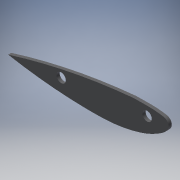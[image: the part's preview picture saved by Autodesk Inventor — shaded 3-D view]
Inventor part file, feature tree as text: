
AUTODESK INVENTOR PART (.ipt)
format: ipt  version: 2018.2 (Build 222227000, 227)  size: 130,560 bytes
history: native  units: mm
features: extrude x2, sketch x2, other x1, projected_geometry x1
ambient origin geometry x8: Origin, YZ Plane, XZ Plane, XY Plane, X Axis, Y Axis, Z Axis, Center Point
bodies: Body1 (feature_tree)
feature tree (6):
  extrude  "押し出し1"  Depth=4.0mm TaperAngle=0.0deg
  extrude  "押し出し2"  Depth=12.0mm
  other  "厚み1"
  sketch  "スケッチ1"
  projected_geometry  "投影ループ1"
  sketch  "スケッチ2"
